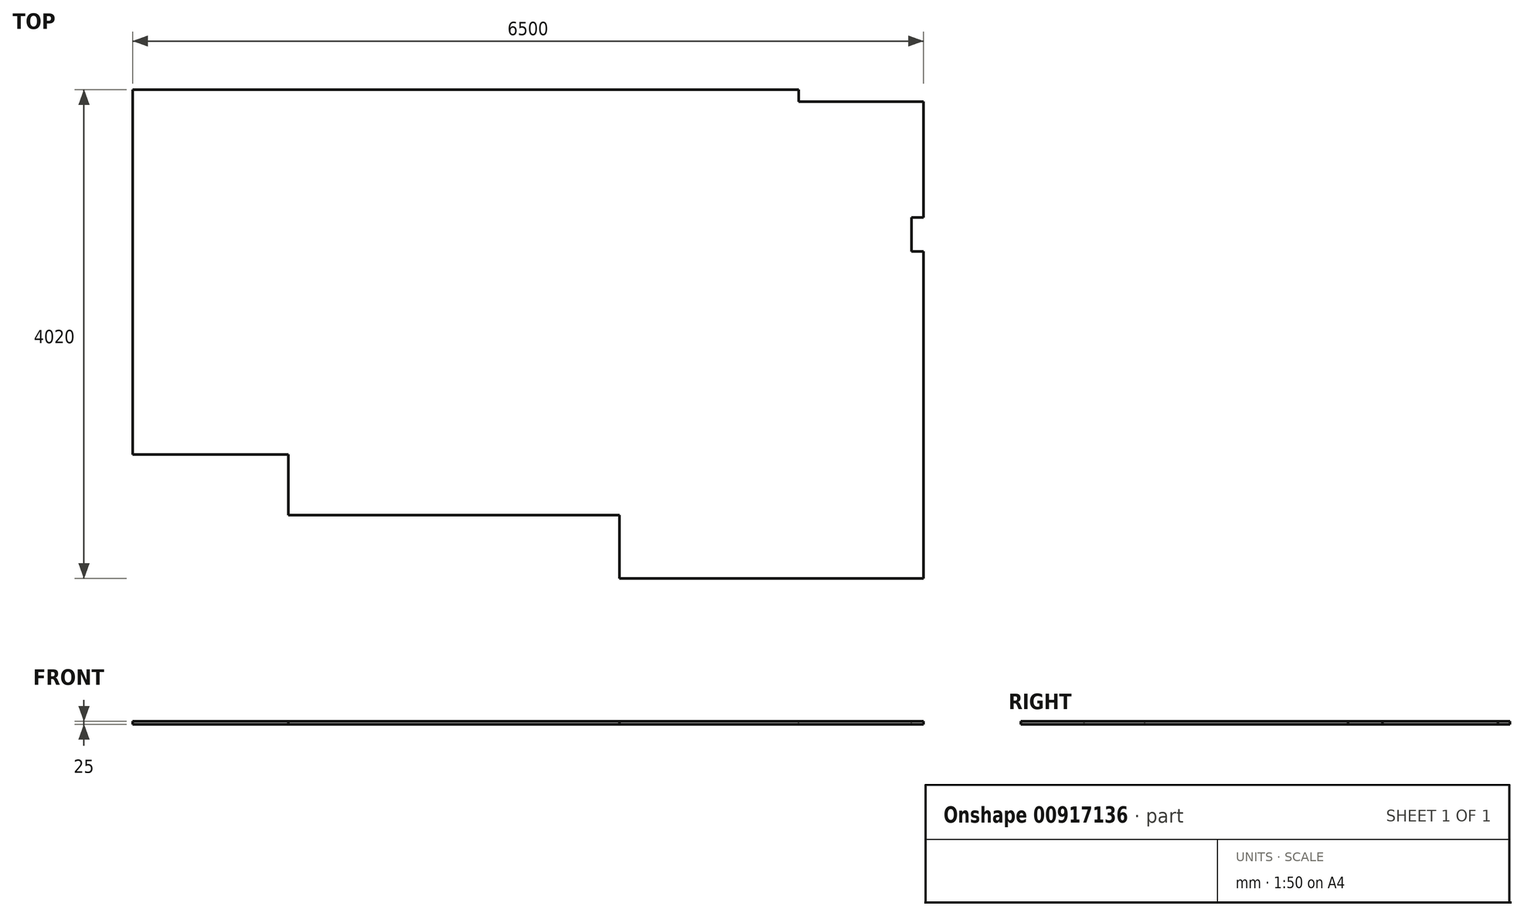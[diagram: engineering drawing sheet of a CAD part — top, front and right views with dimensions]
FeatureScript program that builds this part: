
annotation { "Feature Type Name" : "Feature", "Feature Type Description" : "" }
export const myFeature = defineFeature(function(context is Context, id is Id, definition is map)
    precondition{}
    {
        {
            var Q0;
            Q0=qCreatedBy(makeId("Top.planeOp"),FACE);
            var sketch = newSketch(context, id + "F0", { "sketchPlane" : qUnion([Q0])});
            skLineSegment(sketch, "E0", {"start": v(0, 0) * mm, "end": v(-1025, 0) * mm});
            skLineSegment(sketch, "E1", {"start": v(-1025, 0) * mm, "end": v(-1025, 100) * mm});
            skLineSegment(sketch, "E2", {"start": v(0, 0) * mm, "end": v(0, -950) * mm});
            skLineSegment(sketch, "E3", {"start": v(0, -950) * mm, "end": v(-100, -950) * mm});
            skLineSegment(sketch, "E4", {"start": v(-100, -950) * mm, "end": v(-100, -1230) * mm});
            skLineSegment(sketch, "E5", {"start": v(-100, -1230) * mm, "end": v(0, -1230) * mm});
            skLineSegment(sketch, "E6", {"start": v(0, -1230) * mm, "end": v(0, -3920) * mm});
            skLineSegment(sketch, "E7", {"start": v(0, -3920) * mm, "end": v(-2500, -3920) * mm});
            skLineSegment(sketch, "E8", {"start": v(-1025, 100) * mm, "end": v(-6500, 100) * mm});
            skLineSegment(sketch, "E9", {"start": v(-6500, 100) * mm, "end": v(-6500, -2900) * mm});
            skLineSegment(sketch, "E10", {"start": v(-2500, -3920) * mm, "end": v(-2500, -3400) * mm});
            skLineSegment(sketch, "E11", {"start": v(-2500, -3400) * mm, "end": v(-5220, -3400) * mm});
            skLineSegment(sketch, "E12", {"start": v(-5220, -3400) * mm, "end": v(-5220, -2900) * mm});
            skLineSegment(sketch, "E13", {"start": v(-5220, -2900) * mm, "end": v(-6500, -2900) * mm});
            skSolve(sketch);
        }
        {
            var Q0;
            Q0 = qSketchRegion(id + "F0", true);
            extrude(context, id + "F1", {"entities" : qUnion([Q0]), "oppositeDirection" : true, "depth" : 25 * mm, "offsetDistance" : 25 * mm});
        }
    });
